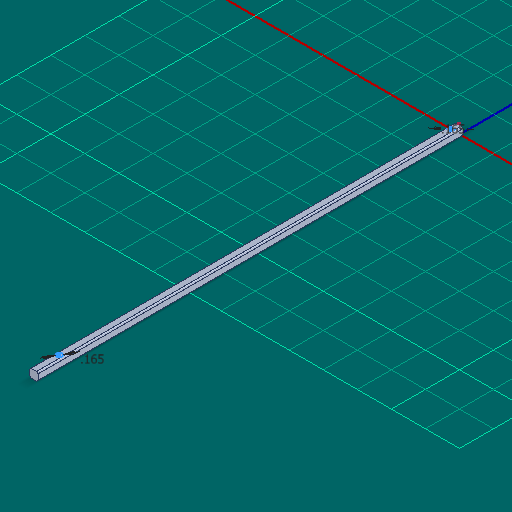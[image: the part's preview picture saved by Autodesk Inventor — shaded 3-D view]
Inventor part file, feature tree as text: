
AUTODESK INVENTOR PART (.ipt)
format: ipt  version: 2025 (Build 290162000, 162)  size: 184,832 bytes
history: native  units: in
note: dims shown in document units (in); Inventor stores cm internally (conversion verified against a paired STEP export)
features: other x50, sketch x3, extrude x2, thicken_offset x1
ambient origin geometry x8: Origin, YZ Plane, XZ Plane, XY Plane, X Axis, Y Axis, Z Axis, Center Point
bodies: Solid1 (feature_tree)
feature tree (56):
  other  "Table"
  other  "Shaft HS 0.5 in"
  other  "Shaft HS 1.0 in"
  other  "Shaft HS 1.5 in"
  other  "Shaft HS 2.0 in"
  other  "Shaft HS 2.5 in"
  other  "Shaft HS 3.0 in"
  other  "Shaft HS 3.5 in"
  other  "Shaft HS 4.0 in"
  other  "Shaft HS 4.5 in"
  other  "Shaft HS 5.0 in"
  other  "Shaft HS 5.5 in"
  other  "Shaft HS 6.0 in"
  other  "Shaft HS 6.5 in"
  other  "Shaft HS 7.0 in"
  other  "Shaft HS 7.5 in"
  other  "Shaft HS 8.0 in"
  other  "Shaft HS 8.5 in"
  other  "Shaft HS 9.0 in"
  other  "Shaft HS 9.5 in"
  other  "Shaft HS 10.0 in"
  other  "Shaft HS 10.5 in"
  other  "Shaft HS 11.0 in"
  other  "Shaft HS 11.5 in"
  other  "Shaft HS 12.0 in"
  other  "Shaft HS 12.5 in"
  other  "Shaft HS 13.0 in"
  other  "Shaft HS 13.5 in"
  other  "Shaft HS 14.0 in"
  other  "Shaft HS 14.5 in"
  other  "Shaft HS 15.0 in"
  other  "Shaft HS 15.5 in"
  other  "Shaft HS 16.0 in"
  other  "Shaft HS 16.5 in"
  other  "Shaft HS 17.0 in"
  other  "Shaft HS 17.5 in"
  other  "Shaft HS 18.0 in"
  other  "Shaft HS 18.5 in"
  other  "Shaft HS 19.0 in"
  other  "Shaft HS 19.5 in"
  other  "Shaft HS 20.0 in"
  other  "Shaft HS 20.5 in"
  other  "Shaft HS 21.0 in"
  other  "Shaft HS 21.5 in"
  other  "Shaft HS 22.0 in"
  other  "Shaft HS 22.5 in"
  other  "Shaft HS 23.0 in"
  other  "Shaft HS 23.5 in"
  other  "Shaft HS 24.0 in"
  extrude  "Extrusion1"  Depth=12.1875in
  thicken_offset  "Thicken1"
  extrude  "Extrusion2"  Depth=11.625in
  sketch  "Sketch4"  dims[d5=0.0in d6=0.165in d7=0.165in]
  sketch  "Sketch2"  dims[d0=0.0625in d1=0.0in d2=12.1875in]
  sketch  "Sketch3"  dims[d3=12.125in d4=11.625in]
  other  "Cut-Revolve3"
